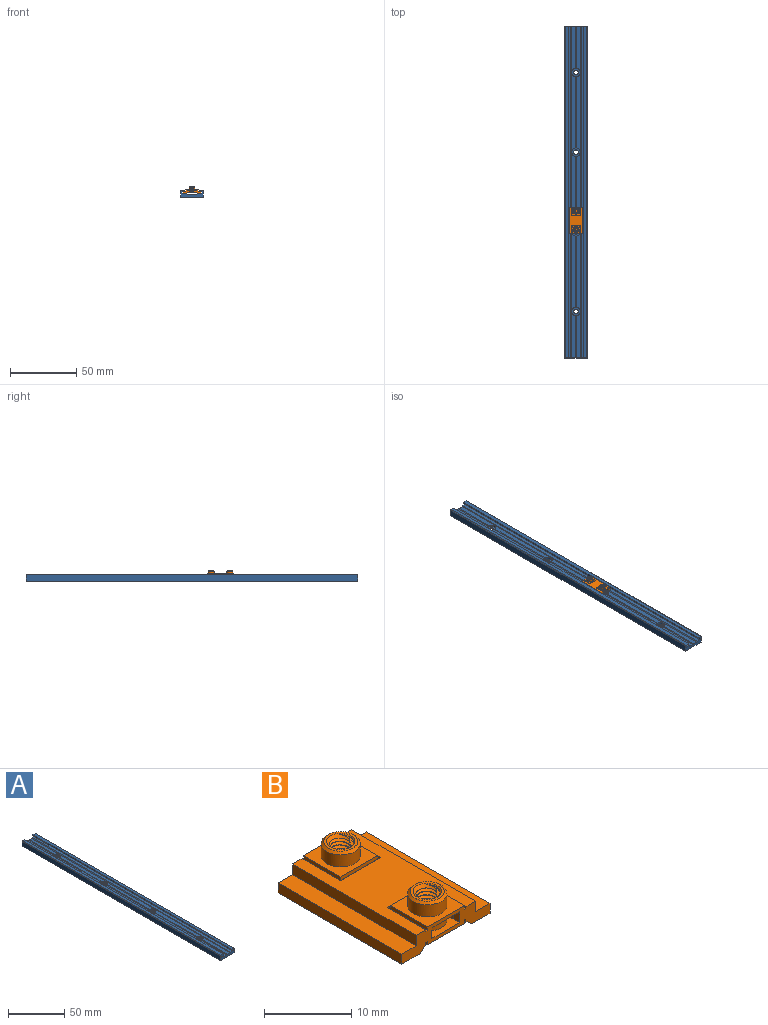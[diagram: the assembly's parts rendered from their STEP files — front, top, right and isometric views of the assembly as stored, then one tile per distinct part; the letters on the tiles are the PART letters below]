
ASSEMBLY  parts=2 mates=1
PART A: 43 faces, bbox 17x250x5.5 mm
  f0: plane 250x17mm, normal (0,0,-1), area 4211.5mm2, adj f14,f15,f29,f30,f33,f36,f39,f42
  f1: plane 250x3.25mm, normal (0,0,1), area 759.1mm2, adj f2,f3,f7,f9,f11,f22,f29,f30
  f2: plane 53.58x0.5mm, normal (-0.5,0,0.87), area 30.9mm2, adj f1,f5,f37,f40
  f3: plane 31.79x0.5mm, normal (-0.5,0,0.87), area 18.3mm2, adj f1,f4,f30,f40
  f4: plane 31.79x0.5mm, normal (0.5,0,0.87), area 18.3mm2, adj f3,f6,f30,f40
  f5: plane 53.58x0.5mm, normal (0.5,0,0.87), area 30.9mm2, adj f2,f6,f37,f40
  f6: plane 250x3.25mm, normal (0,0,1), area 759.1mm2, adj f4,f5,f8,f10,f12,f23,f29,f30
  f7: plane 53.58x0.5mm, normal (-0.5,0,0.87), area 30.9mm2, adj f1,f8,f34,f37
  f8: plane 53.58x0.5mm, normal (0.5,0,0.87), area 30.9mm2, adj f6,f7,f34,f37
  f9: plane 53.58x0.5mm, normal (-0.5,0,0.87), area 30.9mm2, adj f1,f10,f31,f34
  f10: plane 53.58x0.5mm, normal (0.5,0,0.87), area 30.9mm2, adj f6,f9,f31,f34
  f11: plane 31.79x0.5mm, normal (-0.5,0,0.87), area 18.3mm2, adj f1,f12,f29,f31
  f12: plane 31.79x0.5mm, normal (0.5,0,0.87), area 18.3mm2, adj f6,f11,f29,f31
  f13: cylinder r=0.5mm len=250mm, axis (0,1,0), area 196.3mm2, adj f14,f28,f29,f30
  f14: plane 250x5mm, normal (-1,0,0), area 1250mm2, adj f0,f13,f29,f30
  f15: plane 250x5mm, normal (1,0,0), area 1250mm2, adj f0,f16,f29,f30
  f16: cylinder r=0.5mm len=250mm, axis (0,1,0), area 196.3mm2, adj f15,f17,f29,f30
  f17: plane 250x2.7mm, normal (0,0,1), area 675mm2, adj f16,f18,f29,f30
  f18: plane 250x1.2mm, normal (-1,0,0), area 300mm2, adj f17,f19,f29,f30
  f19: plane 250x2mm, normal (0,0,-1), area 500mm2, adj f18,f20,f29,f30
  f20: plane 250x1.5mm, normal (-1,0,0), area 375mm2, adj f19,f21,f29,f30
  f21: plane 250x3.05mm, normal (0,0,1), area 762.5mm2, adj f20,f22,f29,f30
  f22: plane 250x0.5mm, normal (-0.71,0,0.71), area 176.8mm2, adj f1,f21,f29,f30
  f23: plane 250x0.5mm, normal (0.71,0,0.71), area 176.8mm2, adj f6,f24,f29,f30
  f24: plane 250x3.05mm, normal (0,0,1), area 762.5mm2, adj f23,f25,f29,f30
  f25: plane 250x1.5mm, normal (1,0,0), area 375mm2, adj f24,f26,f29,f30
  f26: plane 250x2mm, normal (0,0,-1), area 500mm2, adj f25,f27,f29,f30
  f27: plane 250x1.2mm, normal (1,0,0), area 300mm2, adj f26,f28,f29,f30
  f28: plane 250x2.7mm, normal (0,0,1), area 675mm2, adj f13,f27,f29,f30
  f29: plane 17x5.5mm, normal (0,-1,0), area 54.6mm2, adj f0,f1,f6,f11,f12,f13,f14,f15
  f30: plane 17x5.5mm, normal (0,1,0), area 54.6mm2, adj f0,f1,f3,f4,f6,f13,f14,f15
  f31: cylinder r=3.25mm len=6.5mm, axis (0,0,-1), area 26.3mm2, adj f1,f6,f9,f10,f11,f12,f32
  f32: plane 6.5x6.5mm, normal (0,0,1), area 23.6mm2, adj f31,f33
  f33: cylinder r=1.75mm len=3.5mm, axis (0,0,-1), area 11mm2, adj f0,f32
  f34: cylinder r=3.25mm len=6.5mm, axis (0,0,-1), area 26.3mm2, adj f1,f6,f7,f8,f9,f10,f35
  f35: plane 6.5x6.5mm, normal (0,0,1), area 23.6mm2, adj f34,f36
  f36: cylinder r=1.75mm len=3.5mm, axis (0,0,-1), area 11mm2, adj f0,f35
  f37: cylinder r=3.25mm len=6.5mm, axis (0,0,-1), area 26.3mm2, adj f1,f2,f5,f6,f7,f8,f38
  f38: plane 6.5x6.5mm, normal (0,0,1), area 23.6mm2, adj f37,f39
  f39: cylinder r=1.75mm len=3.5mm, axis (0,0,-1), area 11mm2, adj f0,f38
  f40: cylinder r=3.25mm len=6.5mm, axis (0,0,-1), area 26.3mm2, adj f1,f2,f3,f4,f5,f6,f41
  f41: plane 6.5x6.5mm, normal (0,0,1), area 23.6mm2, adj f40,f42
  f42: cylinder r=1.75mm len=3.5mm, axis (0,0,-1), area 11mm2, adj f0,f41
PART B: 78 faces, bbox 14.4x20.1x5.3 mm
  f0: plane 6x6mm, normal (0,0,-1), area 27.8mm2, adj f5,f6,f7,f47,f77
  f1: plane 6x6mm, normal (0,0,-1), area 27.8mm2, adj f2,f3,f4,f49,f71
  f2: plane 6x0.5mm, normal (-1,0,0), area 3mm2, adj f1,f3,f9,f49
  f3: plane 6x0.5mm, normal (0,1,0), area 3mm2, adj f1,f2,f4,f9
  f4: plane 6x0.5mm, normal (1,0,0), area 3mm2, adj f1,f3,f9,f49
  f5: plane 6x0.5mm, normal (1,0,0), area 3mm2, adj f0,f6,f10,f47
  f6: plane 6x0.5mm, normal (0,-1,0), area 3mm2, adj f0,f5,f7,f10
  f7: plane 6x0.5mm, normal (-1,0,0), area 3mm2, adj f0,f6,f10,f47
  f8: plane 4.52x1.98mm, normal (0,0,1), area 5.1mm2, adj f12,f27,f31,f35,f39,f47
  f9: plane 6.5x6.25mm, normal (0,0,-1), area 4.6mm2, adj f2,f3,f4,f14,f15,f16,f49
  f10: plane 6.5x6.25mm, normal (0,0,-1), area 4.6mm2, adj f5,f6,f7,f17,f18,f19,f47
  f11: plane 4.52x1.98mm, normal (0,0,1), area 5.1mm2, adj f20,f28,f32,f36,f40,f49
  f12: cylinder r=2.25mm len=3.99mm, axis (0,0,-1), area 7.3mm2, adj f8,f22,f27,f31
  f13: plane 3.95x3.95mm, normal (0,0,1), area 3.7mm2, adj f23,f76
  f14: plane 6.25x0.45mm, normal (-1,0,0), area 2.8mm2, adj f9,f15,f24,f49
  f15: plane 6.5x0.45mm, normal (0,-1,0), area 2.9mm2, adj f9,f14,f16,f24
  f16: plane 6.25x0.45mm, normal (1,0,0), area 2.8mm2, adj f9,f15,f24,f49
  f17: plane 6.25x0.45mm, normal (1,0,0), area 2.8mm2, adj f10,f18,f24,f47
  f18: plane 6.5x0.45mm, normal (0,1,0), area 2.9mm2, adj f10,f17,f19,f24
  f19: plane 6.25x0.45mm, normal (-1,0,0), area 2.8mm2, adj f10,f18,f24,f47
  f20: cylinder r=2.25mm len=3.99mm, axis (0,0,-1), area 7.3mm2, adj f11,f25,f28,f32
  f21: plane 3.95x3.95mm, normal (0,0,1), area 3.7mm2, adj f26,f70
  f22: plane 4.52x1.98mm, normal (0,0,-1), area 5.1mm2, adj f12,f27,f31,f35,f39,f47
  f23: cone r=2.25mm half-angle=45deg, axis (0,0,-1), area 5.6mm2, adj f13,f30
  f24: plane 20x6.9mm, normal (0,0,-1), area 56.7mm2, adj f14,f15,f16,f17,f18,f19,f29,f33
  f25: plane 4.52x1.98mm, normal (0,0,-1), area 5.1mm2, adj f20,f28,f32,f36,f40,f49
  f26: cone r=2.25mm half-angle=45deg, axis (0,0,-1), area 5.6mm2, adj f21,f34
  f27: plane 1.5x0.96mm, normal (-0.97,0.26,0), area 1.5mm2, adj f8,f12,f22,f35
  f28: plane 1.5x0.96mm, normal (-0.97,-0.26,0), area 1.5mm2, adj f11,f20,f25,f36
  f29: plane 20x0.7mm, normal (-0.71,0,-0.71), area 19.8mm2, adj f24,f37,f47,f49
  f30: cylinder r=2.25mm len=4.5mm, axis (0,0,-1), area 24mm2, adj f23,f38
  f31: plane 1.5x0.96mm, normal (0.97,0.26,0), area 1.5mm2, adj f8,f12,f22,f39
  f32: plane 1.5x0.96mm, normal (0.97,-0.26,0), area 1.5mm2, adj f11,f20,f25,f40
  f33: plane 20x0.7mm, normal (0.71,0,-0.71), area 19.8mm2, adj f24,f41,f47,f49
  f34: cylinder r=2.25mm len=4.5mm, axis (0,0,-1), area 24mm2, adj f26,f42
  f35: plane 1.5x1mm, normal (-1,0,0), area 1.5mm2, adj f8,f22,f27,f47
  f36: plane 1.5x1mm, normal (-1,0,0), area 1.5mm2, adj f11,f25,f28,f49
  f37: plane 20x3mm, normal (0,0,-1), area 60mm2, adj f29,f43,f47,f49
  f38: plane 6.06x6.06mm, normal (0,0,1), area 20.1mm2, adj f30,f44,f45,f46,f47
  f39: plane 1.5x1mm, normal (1,0,0), area 1.5mm2, adj f8,f22,f31,f47
  f40: plane 1.5x1mm, normal (1,0,0), area 1.5mm2, adj f11,f25,f32,f49
  f41: plane 20x3mm, normal (0,0,-1), area 60mm2, adj f33,f47,f48,f49
  f42: plane 6.06x6.06mm, normal (0,0,1), area 20.1mm2, adj f34,f49,f50,f51,f52
  f43: plane 20x1.4mm, normal (1,0,0), area 28mm2, adj f37,f47,f49,f53
  f44: plane 6x0.5mm, normal (1,0,0), area 3mm2, adj f38,f45,f47,f54
  f45: plane 6x0.5mm, normal (0,-1,0), area 3mm2, adj f38,f44,f46,f54
  f46: plane 6x0.5mm, normal (-1,0,0), area 3mm2, adj f38,f45,f47,f54
  f47: plane 14.3x3.15mm, normal (0,1,0), area 23.7mm2, adj f0,f5,f7,f8,f10,f17,f19,f22
  f48: plane 20x1.4mm, normal (-1,0,0), area 28mm2, adj f41,f47,f49,f55
  f49: plane 14.3x3.15mm, normal (0,-1,0), area 23.7mm2, adj f1,f2,f4,f9,f11,f14,f16,f24
  f50: plane 6x0.5mm, normal (-1,0,0), area 3mm2, adj f42,f49,f51,f56
  f51: plane 6x0.5mm, normal (0,1,0), area 3mm2, adj f42,f50,f52,f56
  f52: plane 6x0.5mm, normal (1,0,0), area 3mm2, adj f42,f49,f51,f56
  f53: plane 20x2.35mm, normal (0,0,1), area 47mm2, adj f43,f47,f49,f58
  f54: plane 6.5x6.25mm, normal (0,0,1), area 4.6mm2, adj f44,f45,f46,f47,f59,f60,f61
  f55: plane 20x2.35mm, normal (0,0,1), area 47mm2, adj f47,f48,f49,f62
  f56: plane 6.5x6.25mm, normal (0,0,1), area 4.6mm2, adj f49,f50,f51,f52,f57,f63,f64
  f57: plane 6.25x0.23mm, normal (-1,0,0), area 1.4mm2, adj f49,f56,f64,f65
  f58: plane 20x1.48mm, normal (1,0,0), area 29.6mm2, adj f47,f49,f53,f65
  f59: plane 6.25x0.23mm, normal (-1,0,0), area 1.4mm2, adj f47,f54,f60,f65
  f60: plane 6.5x0.23mm, normal (0,1,0), area 1.5mm2, adj f54,f59,f61,f65
  f61: plane 6.25x0.23mm, normal (1,0,0), area 1.4mm2, adj f47,f54,f60,f65
  f62: plane 20x1.48mm, normal (-1,0,0), area 29.6mm2, adj f47,f49,f55,f65
  f63: plane 6.25x0.23mm, normal (1,0,0), area 1.4mm2, adj f49,f56,f64,f65
  f64: plane 6.5x0.23mm, normal (0,-1,0), area 1.5mm2, adj f56,f57,f63,f65
  f65: plane 20x9.6mm, normal (0,0,1), area 110.7mm2, adj f47,f49,f57,f58,f59,f60,f61,f62
  f66: cylinder r=1.5mm len=4.26mm, axis (0,0,1), area 5.1mm2, adj f67,f69,f70,f71
  f67: bspline ~4.52x3.46mm, area 25mm2, adj f66,f68,f70,f71
  f68: cylinder r=1.18mm len=3.61mm, axis (0,0,-1), area 5.9mm2, adj f67,f69,f70,f71
  f69: bspline ~4.52x3.46mm, area 25.1mm2, adj f66,f68,f70,f71
  f70: cone r=1.62mm half-angle=45deg, axis (0,0,1), area 3.7mm2, adj f21,f66,f67,f68,f69
  f71: cone r=1.62mm half-angle=45deg, axis (0,0,-1), area 3.7mm2, adj f1,f66,f67,f68,f69
  f72: cylinder r=1.5mm len=4.26mm, axis (0,0,1), area 5.1mm2, adj f73,f75,f76,f77
  f73: bspline ~4.52x3.46mm, area 25mm2, adj f72,f74,f76,f77
  f74: cylinder r=1.18mm len=3.61mm, axis (0,0,-1), area 5.9mm2, adj f73,f75,f76,f77
  f75: bspline ~4.52x3.46mm, area 25.1mm2, adj f72,f74,f76,f77
  f76: cone r=1.62mm half-angle=45deg, axis (0,0,1), area 3.7mm2, adj f13,f72,f73,f74,f75
  f77: cone r=1.62mm half-angle=45deg, axis (0,0,-1), area 3.7mm2, adj f0,f72,f73,f74,f75
PLACE A t=(-31.7,0.51,29.6)mm fixed
PLACE B t=(-31.7,-20.83,29.65)mm
MATE slider B.f49 <-> A.f29  axis (0,-1,0) through (-38.85,-30.83,32.45)mm
